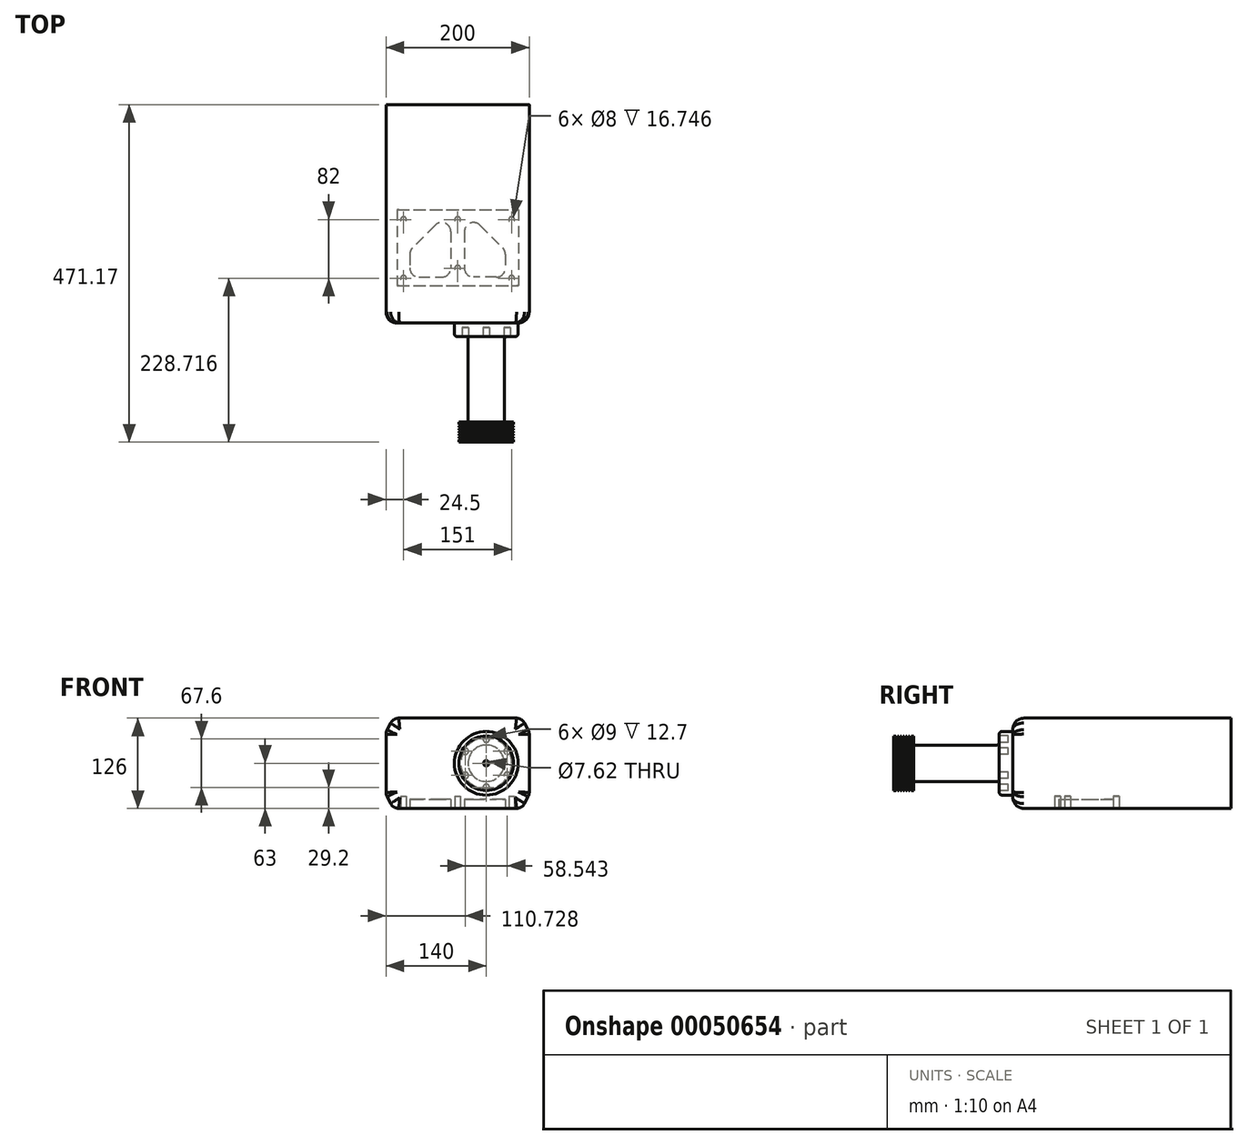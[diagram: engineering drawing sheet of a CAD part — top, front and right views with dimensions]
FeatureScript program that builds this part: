
annotation { "Feature Type Name" : "Feature", "Feature Type Description" : "" }
export const myFeature = defineFeature(function(context is Context, id is Id, definition is map)
    precondition{}
    {
        {
            var Q0;
            Q0=qCreatedBy(makeId("Front.planeOp"),FACE);
            var sketch = newSketch(context, id + "F0", { "sketchPlane" : qUnion([Q0])});
            skLineSegment(sketch, "E0.bottom", {"start": v(-89.84, 63) * mm, "end": v(89.84, 63) * mm});
            skLineSegment(sketch, "E0.top", {"start": v(-89.84, -63) * mm, "end": v(89.84, -63) * mm});
            skLineSegment(sketch, "E0.left", {"start": v(-100, 43.95) * mm, "end": v(-100, -43.95) * mm});
            skLineSegment(sketch, "E0.right", {"start": v(100, 43.95) * mm, "end": v(100, -43.95) * mm});
            skPoint(sketch, "E1", {"position": v(0, 63) * mm});
            skPoint(sketch, "E2", {"position": v(100, 0) * mm});
            skPoint(sketch, "E3.visualSharp", {"position": v(-100, 63) * mm});
            skPoint(sketch, "E4.visualSharp", {"position": v(-100, -63) * mm});
            skPoint(sketch, "E5.visualSharp", {"position": v(100, -63) * mm});
            skPoint(sketch, "E6.visualSharp", {"position": v(100, 63) * mm});
            skLineSegment(sketch, "E7", {"start": v(-100, -43.95) * mm, "end": v(-89.84, -63) * mm});
            skLineSegment(sketch, "E8", {"start": v(89.84, -63) * mm, "end": v(100, -43.95) * mm});
            skLineSegment(sketch, "E9", {"start": v(-100, 43.95) * mm, "end": v(-89.84, 63) * mm});
            skLineSegment(sketch, "E10", {"start": v(89.84, 63) * mm, "end": v(100, 43.95) * mm});
            skSolve(sketch);
        }
        {
            var Q0;
            Q0=makeQuery(id+"F0.imprint","IMPRINT",FACE,{"disambiguationData":[TD([[makeQuery(id+"F0.imprint","IMPRINT",EDGE,{"derivedFrom":sQuery(id+"F0.wireOp",EDGE,"E0.bottom")}),-1.0]])]});
            extrude(context, id + "F1", {"entities" : qUnion([Q0]), "oppositeDirection" : true, "depth" : 304.8 * mm});
        }
        {
            var Q0;
            Q0=makeQuery(id+"F1.opExtrude","SWEPT_EDGE",EDGE,{"disambiguationData":[OSD([sQuery(id+"F0.wireOp",EDGE,"E0.left"),sQuery(id+"F0.wireOp",EDGE,"E9")])]});
            var Q1;
            Q1=makeQuery(id+"F1.opExtrude","SWEPT_EDGE",EDGE,{"disambiguationData":[OSD([sQuery(id+"F0.wireOp",EDGE,"E0.left"),sQuery(id+"F0.wireOp",EDGE,"E7")])]});
            var Q2;
            Q2=makeQuery(id+"F1.opExtrude","SWEPT_EDGE",EDGE,{"disambiguationData":[OSD([sQuery(id+"F0.wireOp",EDGE,"E0.right"),sQuery(id+"F0.wireOp",EDGE,"E10")])]});
            var Q3;
            Q3=makeQuery(id+"F1.opExtrude","SWEPT_EDGE",EDGE,{"disambiguationData":[OSD([sQuery(id+"F0.wireOp",EDGE,"E0.right"),sQuery(id+"F0.wireOp",EDGE,"E8")])]});
            var Q4;
            Q4=makeQuery(id+"F1.opExtrude","SWEPT_EDGE",EDGE,{"disambiguationData":[OSD([sQuery(id+"F0.wireOp",EDGE,"E0.bottom"),sQuery(id+"F0.wireOp",EDGE,"E9")])]});
            var Q5;
            Q5=makeQuery(id+"F1.opExtrude","SWEPT_EDGE",EDGE,{"disambiguationData":[OSD([sQuery(id+"F0.wireOp",EDGE,"E0.bottom"),sQuery(id+"F0.wireOp",EDGE,"E10")])]});
            var Q6;
            Q6=makeQuery(id+"F1.opExtrude","SWEPT_EDGE",EDGE,{"disambiguationData":[OSD([sQuery(id+"F0.wireOp",EDGE,"E0.top"),sQuery(id+"F0.wireOp",EDGE,"E7")])]});
            var Q7;
            Q7=makeQuery(id+"F1.opExtrude","SWEPT_EDGE",EDGE,{"disambiguationData":[OSD([sQuery(id+"F0.wireOp",EDGE,"E0.top"),sQuery(id+"F0.wireOp",EDGE,"E8")])]});
            fillet(context, id + "F2", {"entities" : qUnion([Q0, Q1, Q2, Q3, Q4, Q5, Q6, Q7]), "radius" : 12.7 * mm, "tangentPropagation" : true, "allowEdgeOverflow" : false});
        }
        {
            var Q0;
            Q0=qCreatedBy(makeId("Right.planeOp"),FACE);
            cPlane(context, id + "F3", {"entities" : qUnion([Q0]), "cplaneType" : CPlaneType.OFFSET, "offset" : 40 * mm, "width" : 152.4 * mm, "height" : 152.4 * mm});
        }
        {
            var Q0;
            Q0=qCreatedBy(id+"F3.planeOp",FACE);
            var sketch = newSketch(context, id + "F4", { "sketchPlane" : qUnion([Q0])});
            skLineSegment(sketch, "E11.bottom", {"start": v(0, 44.45) * mm, "end": v(-19.05, 44.45) * mm});
            skLineSegment(sketch, "E11.left", {"start": v(0, 44.45) * mm, "end": v(0, 0) * mm});
            skLineSegment(sketch, "E11.right", {"start": v(-19.05, 44.45) * mm, "end": v(-19.05, 25.4) * mm});
            skLineSegment(sketch, "E12.bottom", {"start": v(-19.05, 25.4) * mm, "end": v(-138.43, 25.4) * mm});
            skLineSegment(sketch, "E13.bottom", {"start": v(-138.43, 38.1) * mm, "end": v(-166.37, 38.1) * mm, "construction": true});
            skLineSegment(sketch, "E13.left", {"start": v(-138.43, 38.1) * mm, "end": v(-138.43, 25.4) * mm});
            skLineSegment(sketch, "E13.right", {"start": v(-166.37, 38.1) * mm, "end": v(-166.37, 3.8) * mm});
            skLineSegment(sketch, "E14", {"start": v(-168.35, 35.56) * mm, "end": v(-138.73, 35.56) * mm, "construction": true});
            skLineSegment(sketch, "E15", {"start": v(-163.2, 38.1) * mm, "end": v(-162.18, 35.56) * mm});
            skLineSegment(sketch, "E16", {"start": v(-162.18, 35.56) * mm, "end": v(-161.67, 35.56) * mm});
            skLineSegment(sketch, "E17", {"start": v(-161.67, 35.56) * mm, "end": v(-160.65, 38.1) * mm});
            skPoint(sketch, "E18", {"position": v(-161.92, 35.56) * mm});
            skLineSegment(sketch, "E19", {"start": v(-163.2, 38.1) * mm, "end": v(-160.65, 38.1) * mm, "construction": true});
            skPoint(sketch, "E20", {"position": v(-161.92, 38.1) * mm});
            skLineSegment(sketch, "E21", {"start": v(-161.92, 35.56) * mm, "end": v(-161.92, 38.1) * mm, "construction": true});
            skLineSegment(sketch, "E22.1.0.0", {"start": v(-159.38, 38.1) * mm, "end": v(-156.84, 38.1) * mm, "construction": true});
            skLineSegment(sketch, "E22.1.0.1", {"start": v(-158.11, 35.56) * mm, "end": v(-158.11, 38.1) * mm, "construction": true});
            skLineSegment(sketch, "E22.1.0.2", {"start": v(-157.86, 35.56) * mm, "end": v(-156.84, 38.1) * mm});
            skPoint(sketch, "E22.1.0.3", {"position": v(-158.11, 38.1) * mm});
            skPoint(sketch, "E22.1.0.4", {"position": v(-158.11, 35.56) * mm});
            skLineSegment(sketch, "E22.1.0.5", {"start": v(-159.38, 38.1) * mm, "end": v(-158.37, 35.56) * mm});
            skLineSegment(sketch, "E22.1.0.6", {"start": v(-158.37, 35.56) * mm, "end": v(-157.86, 35.56) * mm});
            skLineSegment(sketch, "E22.1.0.7", {"start": v(-158.37, 35.56) * mm, "end": v(-157.86, 35.56) * mm});
            skLineSegment(sketch, "E22.2.0.0", {"start": v(-155.57, 38.1) * mm, "end": v(-153.03, 38.1) * mm, "construction": true});
            skLineSegment(sketch, "E22.2.0.1", {"start": v(-154.3, 35.56) * mm, "end": v(-154.3, 38.1) * mm, "construction": true});
            skLineSegment(sketch, "E22.2.0.2", {"start": v(-154.05, 35.56) * mm, "end": v(-153.03, 38.1) * mm});
            skPoint(sketch, "E22.2.0.3", {"position": v(-154.3, 38.1) * mm});
            skPoint(sketch, "E22.2.0.4", {"position": v(-154.3, 35.56) * mm});
            skLineSegment(sketch, "E22.2.0.5", {"start": v(-155.58, 38.1) * mm, "end": v(-154.56, 35.56) * mm});
            skLineSegment(sketch, "E22.2.0.6", {"start": v(-154.56, 35.56) * mm, "end": v(-154.05, 35.56) * mm});
            skLineSegment(sketch, "E22.2.0.7", {"start": v(-154.56, 35.56) * mm, "end": v(-154.05, 35.56) * mm});
            skLineSegment(sketch, "E22.3.0.0", {"start": v(-151.77, 38.1) * mm, "end": v(-149.23, 38.1) * mm, "construction": true});
            skLineSegment(sketch, "E22.3.0.1", {"start": v(-150.5, 35.56) * mm, "end": v(-150.5, 38.1) * mm, "construction": true});
            skLineSegment(sketch, "E22.3.0.2", {"start": v(-150.24, 35.56) * mm, "end": v(-149.22, 38.1) * mm});
            skPoint(sketch, "E22.3.0.3", {"position": v(-150.5, 38.1) * mm});
            skPoint(sketch, "E22.3.0.4", {"position": v(-150.5, 35.56) * mm});
            skLineSegment(sketch, "E22.3.0.5", {"start": v(-151.77, 38.1) * mm, "end": v(-150.75, 35.56) * mm});
            skLineSegment(sketch, "E22.3.0.6", {"start": v(-150.75, 35.56) * mm, "end": v(-150.24, 35.56) * mm});
            skLineSegment(sketch, "E22.3.0.7", {"start": v(-150.75, 35.56) * mm, "end": v(-150.24, 35.56) * mm});
            skLineSegment(sketch, "E22.4.0.0", {"start": v(-147.96, 38.1) * mm, "end": v(-145.42, 38.1) * mm, "construction": true});
            skLineSegment(sketch, "E22.4.0.1", {"start": v(-146.68, 35.56) * mm, "end": v(-146.68, 38.1) * mm, "construction": true});
            skLineSegment(sketch, "E22.4.0.2", {"start": v(-146.43, 35.56) * mm, "end": v(-145.41, 38.1) * mm});
            skPoint(sketch, "E22.4.0.3", {"position": v(-146.69, 38.1) * mm});
            skPoint(sketch, "E22.4.0.4", {"position": v(-146.69, 35.56) * mm});
            skLineSegment(sketch, "E22.4.0.5", {"start": v(-147.96, 38.1) * mm, "end": v(-146.94, 35.56) * mm});
            skLineSegment(sketch, "E22.4.0.6", {"start": v(-146.94, 35.56) * mm, "end": v(-146.43, 35.56) * mm});
            skLineSegment(sketch, "E22.4.0.7", {"start": v(-146.94, 35.56) * mm, "end": v(-146.43, 35.56) * mm});
            skLineSegment(sketch, "E22.5.0.0", {"start": v(-144.15, 38.1) * mm, "end": v(-141.6, 38.1) * mm, "construction": true});
            skLineSegment(sketch, "E22.5.0.1", {"start": v(-142.87, 35.56) * mm, "end": v(-142.87, 38.1) * mm, "construction": true});
            skLineSegment(sketch, "E22.5.0.2", {"start": v(-142.62, 35.56) * mm, "end": v(-141.6, 38.1) * mm});
            skPoint(sketch, "E22.5.0.3", {"position": v(-142.88, 38.1) * mm});
            skPoint(sketch, "E22.5.0.4", {"position": v(-142.88, 35.56) * mm});
            skLineSegment(sketch, "E22.5.0.5", {"start": v(-144.15, 38.1) * mm, "end": v(-143.13, 35.56) * mm});
            skLineSegment(sketch, "E22.5.0.6", {"start": v(-143.13, 35.56) * mm, "end": v(-142.62, 35.56) * mm});
            skLineSegment(sketch, "E22.5.0.7", {"start": v(-143.13, 35.56) * mm, "end": v(-142.62, 35.56) * mm});
            skLineSegment(sketch, "E22.direction1", {"start": v(-163.2, 38.1) * mm, "end": v(-159.38, 38.1) * mm, "construction": true});
            skLineSegment(sketch, "E23", {"start": v(-160.65, 38.1) * mm, "end": v(-159.38, 38.1) * mm});
            skLineSegment(sketch, "E24", {"start": v(-156.84, 38.1) * mm, "end": v(-155.57, 38.1) * mm});
            skLineSegment(sketch, "E25", {"start": v(-153.03, 38.1) * mm, "end": v(-151.77, 38.1) * mm});
            skLineSegment(sketch, "E26", {"start": v(-149.23, 38.1) * mm, "end": v(-147.96, 38.1) * mm});
            skLineSegment(sketch, "E27", {"start": v(-145.42, 38.1) * mm, "end": v(-144.15, 38.1) * mm});
            skLineSegment(sketch, "E28", {"start": v(-141.6, 38.1) * mm, "end": v(-138.43, 38.1) * mm});
            skLineSegment(sketch, "E29", {"start": v(-166.37, 38.1) * mm, "end": v(-163.2, 38.1) * mm});
            skPoint(sketch, "E30", {"position": v(-152.4, 38.1) * mm});
            skLineSegment(sketch, "E31", {"start": v(-152.4, 38.1) * mm, "end": v(-152.4, 5.68) * mm, "construction": true});
            skLineSegment(sketch, "E32", {"start": v(-166.37, 3.8) * mm, "end": v(-158.75, 3.8) * mm});
            skLineSegment(sketch, "E33", {"start": v(-158.75, 3.8) * mm, "end": v(-156.21, 0) * mm});
            skPoint(sketch, "E34.orphan", {"position": v(-166.37, 0) * mm});
            skLineSegment(sketch, "E35", {"start": v(-156.21, 0) * mm, "end": v(0, 0) * mm});
            skSolve(sketch);
        }
        {
            var Q0;
            Q0 = qSketchRegion(id + "F4", true);
            var Q1;
            Q1=sQuery(id+"F4.wireOp",EDGE,"E35");
            revolve(context, id + "F5", {"operationType" : NewBodyOperationType.ADD, "entities" : qUnion([Q0]), "axis" : qUnion([Q1]), "revolveType" : RevolveType.FULL});
        }
        {
            var Q0;
            Q0=makeQuery(id+"F5.opRevolve","SWEPT_EDGE",EDGE,{"disambiguationData":[OSD([sQuery(id+"F4.wireOp",EDGE,"E11.right"),sQuery(id+"F4.wireOp",EDGE,"E12.bottom")])]});
            var Q1;
            Q1=makeQuery(id+"F5.opRevolve","SWEPT_EDGE",EDGE,{"disambiguationData":[OSD([sQuery(id+"F4.wireOp",EDGE,"E11.bottom"),sQuery(id+"F4.wireOp",EDGE,"E11.right")])]});
            fillet(context, id + "F6", {"entities" : qUnion([Q0, Q1]), "radius" : 3.8 * mm, "tangentPropagation" : true, "allowEdgeOverflow" : false});
        }
        {
            var Q0;
            Q0=makeQuery(id+"F1.opExtrude","SWEPT_FACE",FACE,{"disambiguationData":[OSD([sQuery(id+"F0.wireOp",EDGE,"E0.top")])]});
            var sketch = newSketch(context, id + "F7", { "sketchPlane" : qUnion([Q0])});
            skLineSegment(sketch, "E36", {"start": v(22.23, -64) * mm, "end": v(53.97, -64) * mm});
            skLineSegment(sketch, "E37", {"start": v(66.67, -76.7) * mm, "end": v(66.67, -95.75) * mm});
            skLineSegment(sketch, "E38", {"start": v(62.96, -104.73) * mm, "end": v(31.2, -136.48) * mm});
            skLineSegment(sketch, "E39", {"start": v(9.52, -76.7) * mm, "end": v(9.53, -127.5) * mm});
            skPoint(sketch, "E40.visualSharp", {"position": v(9.52, -158.16) * mm});
            skArc(sketch, "E40.filletArc", {"start": v(9.53, -127.5) * mm, "mid": v(17.36, -139.23) * mm, "end": v(31.2, -136.48) * mm});
            skPoint(sketch, "E41.visualSharp", {"position": v(9.52, -64) * mm});
            skArc(sketch, "E41.filletArc", {"start": v(22.23, -64) * mm, "mid": v(13.24, -67.72) * mm, "end": v(9.52, -76.7) * mm});
            skPoint(sketch, "E42.visualSharp", {"position": v(66.67, -64) * mm});
            skArc(sketch, "E42.filletArc", {"start": v(66.67, -76.7) * mm, "mid": v(62.96, -67.72) * mm, "end": v(53.97, -64) * mm});
            skPoint(sketch, "E43.visualSharp", {"position": v(66.67, -101.01) * mm});
            skArc(sketch, "E43.filletArc", {"start": v(62.96, -104.73) * mm, "mid": v(65.7, -100.61) * mm, "end": v(66.67, -95.75) * mm});
            skArc(sketch, "E44.MirrorCS", {"start": v(-62.96, -104.73) * mm, "mid": v(-65.7, -100.61) * mm, "end": v(-66.67, -95.75) * mm});
            skPoint(sketch, "E45.MirrorP", {"position": v(-9.52, -158.16) * mm});
            skPoint(sketch, "E46.MirrorP", {"position": v(-66.67, -101.01) * mm});
            skLineSegment(sketch, "E47.MirrorCS", {"start": v(-62.96, -104.73) * mm, "end": v(-31.2, -136.48) * mm});
            skLineSegment(sketch, "E48.MirrorCS", {"start": v(-22.23, -64) * mm, "end": v(-53.97, -64) * mm});
            skArc(sketch, "E49.MirrorCS", {"start": v(-66.67, -76.7) * mm, "mid": v(-62.96, -67.72) * mm, "end": v(-53.97, -64) * mm});
            skLineSegment(sketch, "E50.MirrorCS", {"start": v(-66.67, -76.7) * mm, "end": v(-66.67, -95.75) * mm});
            skLineSegment(sketch, "E51.MirrorCS", {"start": v(-9.52, -76.7) * mm, "end": v(-9.53, -127.5) * mm});
            skArc(sketch, "E52.MirrorCS", {"start": v(-9.53, -127.5) * mm, "mid": v(-17.36, -139.23) * mm, "end": v(-31.2, -136.48) * mm});
            skPoint(sketch, "E53.MirrorP", {"position": v(-66.67, -64) * mm});
            skArc(sketch, "E54.MirrorCS", {"start": v(-22.23, -64) * mm, "mid": v(-13.24, -67.72) * mm, "end": v(-9.52, -76.7) * mm});
            skPoint(sketch, "E55.MirrorP", {"position": v(-9.52, -64) * mm});
            skSolve(sketch);
        }
        {
            var Q0;
            Q0 = qSketchRegion(id + "F7", true);
            extrude(context, id + "F8", {"entities" : qUnion([Q0]), "operationType" : NewBodyOperationType.REMOVE, "oppositeDirection" : true, "depth" : 12.7 * mm});
        }
        {
            var Q0;
            Q0=makeQuery(id+"F1.opExtrude","CAP_EDGE",EDGE,{"disambiguationData":[OSD([sQuery(id+"F0.wireOp",EDGE,"E0.bottom")])],"isStart":true});
            fillet(context, id + "F9", {"entities" : qUnion([Q0]), "radius" : 15.24 * mm, "tangentPropagation" : true, "allowEdgeOverflow" : false});
        }
        {
            var Q0;
            Q0=makeQuery(id+"F1.opExtrude","SWEPT_FACE",FACE,{"disambiguationData":[OSD([sQuery(id+"F0.wireOp",EDGE,"E0.top")])]});
            var sketch = newSketch(context, id + "F10", { "sketchPlane" : qUnion([Q0])});
            skLineSegment(sketch, "E56.bottom", {"start": v(-88.9, -52) * mm, "end": v(88.9, -52) * mm});
            skLineSegment(sketch, "E56.top", {"start": v(-88.9, -158) * mm, "end": v(88.9, -158) * mm});
            skLineSegment(sketch, "E56.left", {"start": v(-88.9, -52) * mm, "end": v(-88.9, -158) * mm});
            skLineSegment(sketch, "E56.right", {"start": v(88.9, -52) * mm, "end": v(88.9, -158) * mm});
            skPoint(sketch, "E57", {"position": v(0, -52) * mm});
            skSolve(sketch);
        }
        {
            var Q0;
            Q0 = qSketchRegion(id + "F10", true);
            extrude(context, id + "F11", {"entities" : qUnion([Q0]), "operationType" : NewBodyOperationType.REMOVE, "oppositeDirection" : true, "depth" : 0.25 * mm});
        }
        {
            var Q0;
            {var subQ2=sQuery(id+"F0.wireOp",EDGE,"E0.top");Q0=makeQuery(id+"F11.boolean.opBoolean","SPLIT",FACE,{"disambiguationData":[TD([makeQuery(id+"F11.opExtrude","SWEPT_FACE",FACE,{"disambiguationData":[OSD([sQuery(id+"F10.wireOp",EDGE,"E56.top")])]})])],"derivedFrom":makeQuery(id+"F1.opExtrude","SWEPT_FACE",FACE,{"disambiguationData":[OSD([subQ2])]})});}
            var sketch = newSketch(context, id + "F12", { "sketchPlane" : qUnion([Q0])});
            skCircle(sketch, "E58", {"center": v(-75.5, -62.35) * mm, "radius": 4 * mm});
            skLineSegment(sketch, "E59", {"start": v(-75.5, -62.35) * mm, "end": v(-75.5, -144.35) * mm, "construction": true});
            skLineSegment(sketch, "E60", {"start": v(-75.5, -144.35) * mm, "end": v(75.5, -144.35) * mm, "construction": true});
            skLineSegment(sketch, "E61", {"start": v(75.5, -144.35) * mm, "end": v(75.5, -62.35) * mm, "construction": true});
            skLineSegment(sketch, "E62", {"start": v(75.5, -62.35) * mm, "end": v(0, -62.35) * mm, "construction": true});
            skLineSegment(sketch, "E63", {"start": v(0, -62.35) * mm, "end": v(0, -76.35) * mm, "construction": true});
            skCircle(sketch, "E64", {"center": v(0, -76.35) * mm, "radius": 4 * mm});
            skCircle(sketch, "E65", {"center": v(-75.5, -144.35) * mm, "radius": 4 * mm});
            skCircle(sketch, "E66", {"center": v(75.5, -144.35) * mm, "radius": 4 * mm});
            skCircle(sketch, "E67", {"center": v(75.5, -62.35) * mm, "radius": 4 * mm});
            skPoint(sketch, "E68", {"position": v(0, -144.35) * mm});
            skCircle(sketch, "E69", {"center": v(0, -144.35) * mm, "radius": 4 * mm});
            skSolve(sketch);
        }
        {
            var Q0;
            Q0 = qSketchRegion(id + "F12", true);
            extrude(context, id + "F13", {"entities" : qUnion([Q0]), "operationType" : NewBodyOperationType.REMOVE, "oppositeDirection" : true, "depth" : 17 * mm});
        }
        {
            var Q0;
            Q0=makeQuery(id+"F5.opRevolve","SWEPT_FACE",FACE,{"disambiguationData":[OSD([sQuery(id+"F4.wireOp",EDGE,"E11.right")])]});
            var sketch = newSketch(context, id + "F14", { "sketchPlane" : qUnion([Q0])});
            skCircle(sketch, "E70", {"center": v(40, 33.8) * mm, "radius": 4.5 * mm});
            skCircle(sketch, "E71.1.0", {"center": v(10.73, 16.9) * mm, "radius": 4.5 * mm});
            skCircle(sketch, "E71.2.0", {"center": v(10.73, -16.9) * mm, "radius": 4.5 * mm});
            skCircle(sketch, "E71.3.0", {"center": v(40, -33.8) * mm, "radius": 4.5 * mm});
            skCircle(sketch, "E71.4.0", {"center": v(69.27, -16.9) * mm, "radius": 4.5 * mm});
            skCircle(sketch, "E71.5.0", {"center": v(69.27, 16.9) * mm, "radius": 4.5 * mm});
            skPoint(sketch, "E71.center", {"position": v(40, 0) * mm});
            skSolve(sketch);
        }
        {
            var Q0;
            Q0 = qSketchRegion(id + "F14", true);
            extrude(context, id + "F15", {"entities" : qUnion([Q0]), "operationType" : NewBodyOperationType.REMOVE, "oppositeDirection" : true, "depth" : 12.7 * mm});
        }
    });
